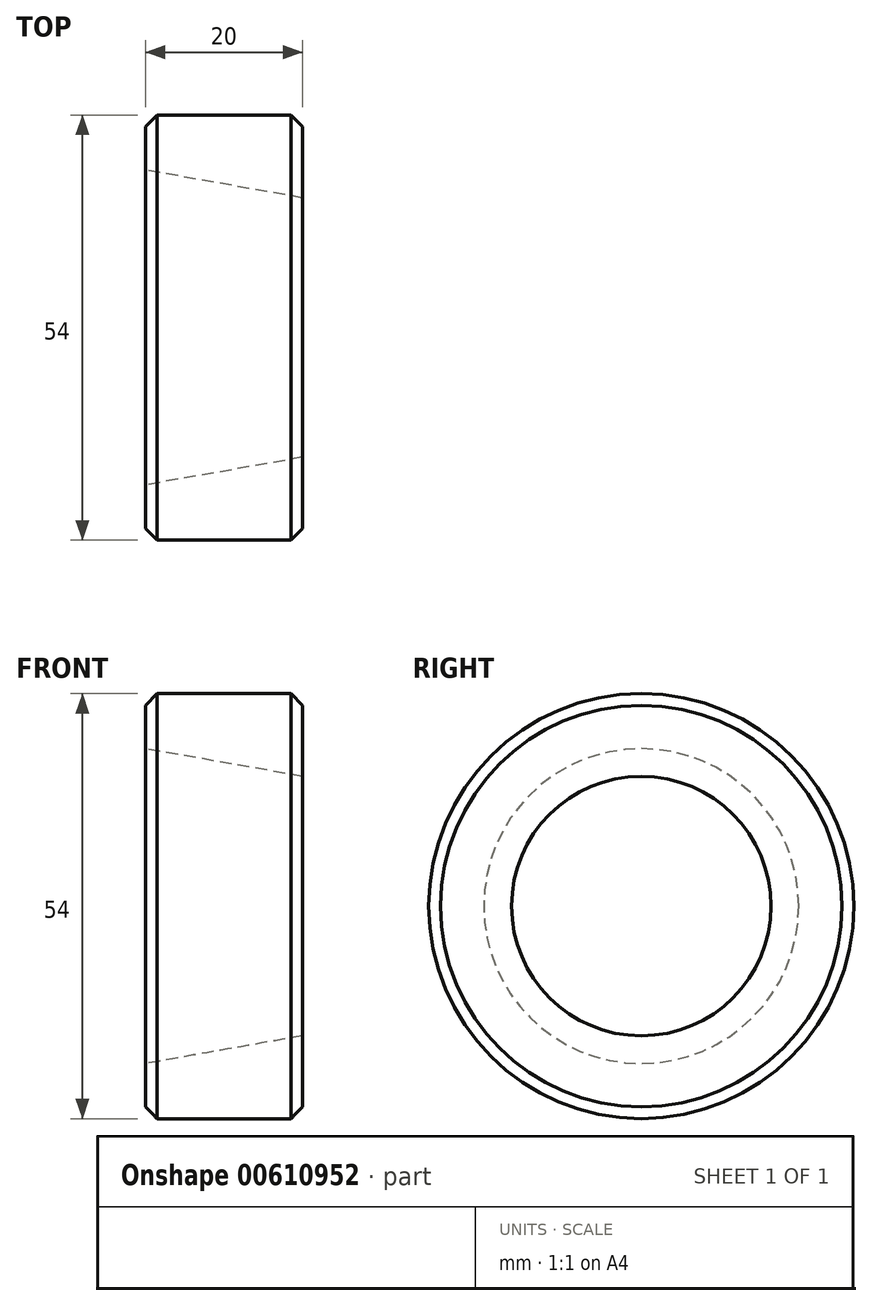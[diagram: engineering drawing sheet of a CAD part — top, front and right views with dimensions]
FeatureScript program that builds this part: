
annotation { "Feature Type Name" : "Feature", "Feature Type Description" : "" }
export const myFeature = defineFeature(function(context is Context, id is Id, definition is map)
    precondition{}
    {
        {
            var Q0;
            Q0=qCreatedBy(makeId("Front.planeOp"),FACE);
            var sketch = newSketch(context, id + "F0", { "sketchPlane" : qUnion([Q0])});
            skLineSegment(sketch, "E0.bottom", {"start": v(0, 0) * mm, "end": v(26, 0) * mm});
            skLineSegment(sketch, "E0.top", {"start": v(0, -15) * mm, "end": v(26, -15) * mm});
            skLineSegment(sketch, "E0.left", {"start": v(0, 0) * mm, "end": v(0, -15) * mm});
            skLineSegment(sketch, "E0.right", {"start": v(26, 0) * mm, "end": v(26, -15) * mm});
            skArc(sketch, "E1", {"start": v(32, -11) * mm, "mid": v(29, -9.02) * mm, "end": v(26, -11) * mm});
            skLineSegment(sketch, "E2.bottom", {"start": v(32, -15) * mm, "end": v(37, -15) * mm});
            skLineSegment(sketch, "E2.top", {"start": v(32, 0) * mm, "end": v(37, 0) * mm});
            skLineSegment(sketch, "E2.left", {"start": v(32, -15) * mm, "end": v(32, 0) * mm});
            skLineSegment(sketch, "E2.right", {"start": v(37, -15) * mm, "end": v(37, 0) * mm});
            skLineSegment(sketch, "E3", {"start": v(26, 0) * mm, "end": v(32, 0) * mm});
            skLineSegment(sketch, "E4.bottom", {"start": v(37, 0) * mm, "end": v(44, 0) * mm});
            skLineSegment(sketch, "E4.top", {"start": v(37, -10) * mm, "end": v(44, -10) * mm});
            skLineSegment(sketch, "E4.left", {"start": v(37, 0) * mm, "end": v(37, -10) * mm});
            skLineSegment(sketch, "E4.right", {"start": v(44, 0) * mm, "end": v(44, -10) * mm});
            skLineSegment(sketch, "E5.right", {"start": v(70, 0) * mm, "end": v(70, -20) * mm});
            skLineSegment(sketch, "E6", {"start": v(70, -20) * mm, "end": v(89, -16.65) * mm});
            skLineSegment(sketch, "E7", {"start": v(89, -16.65) * mm, "end": v(89, 0) * mm});
            skLineSegment(sketch, "E8", {"start": v(89, 0) * mm, "end": v(70, 0) * mm});
            skLineSegment(sketch, "E9.bottom", {"start": v(89, -13) * mm, "end": v(94, -13) * mm});
            skLineSegment(sketch, "E9.top", {"start": v(89, 0) * mm, "end": v(94, 0) * mm});
            skLineSegment(sketch, "E9.left", {"start": v(89, -13) * mm, "end": v(89, 0) * mm});
            skLineSegment(sketch, "E9.right", {"start": v(94, -13) * mm, "end": v(94, 0) * mm});
            skLineSegment(sketch, "E10.bottom", {"start": v(94, 0) * mm, "end": v(120, 0) * mm});
            skLineSegment(sketch, "E10.top", {"start": v(94, -15) * mm, "end": v(120, -15) * mm});
            skLineSegment(sketch, "E10.left", {"start": v(94, 0) * mm, "end": v(94, -15) * mm});
            skLineSegment(sketch, "E10.right", {"start": v(120, 0) * mm, "end": v(120, -15) * mm});
            skLineSegment(sketch, "E11.bottom", {"start": v(44, 0) * mm, "end": v(49, 0) * mm});
            skLineSegment(sketch, "E11.top", {"start": v(44, -15) * mm, "end": v(49, -15) * mm});
            skLineSegment(sketch, "E11.left", {"start": v(44, 0) * mm, "end": v(44, -15) * mm});
            skLineSegment(sketch, "E11.right", {"start": v(49, 0) * mm, "end": v(49, -15) * mm});
            skLineSegment(sketch, "E12.bottom", {"start": v(61, -10) * mm, "end": v(49, -10) * mm});
            skLineSegment(sketch, "E12.top", {"start": v(61, 0) * mm, "end": v(49, 0) * mm});
            skLineSegment(sketch, "E12.left", {"start": v(61, -10) * mm, "end": v(61, 0) * mm});
            skLineSegment(sketch, "E12.right", {"start": v(49, -10) * mm, "end": v(49, 0) * mm});
            skLineSegment(sketch, "E13.bottom", {"start": v(61, 0) * mm, "end": v(66, 0) * mm});
            skLineSegment(sketch, "E13.top", {"start": v(61, -34.36) * mm, "end": v(66, -34.36) * mm});
            skLineSegment(sketch, "E13.left", {"start": v(61, 0) * mm, "end": v(61, -34.36) * mm});
            skLineSegment(sketch, "E13.right", {"start": v(66, 0) * mm, "end": v(66, -34.36) * mm});
            skLineSegment(sketch, "E14.bottom", {"start": v(66, 0) * mm, "end": v(70, 0) * mm});
            skLineSegment(sketch, "E14.top", {"start": v(66, -20) * mm, "end": v(70, -20) * mm});
            skLineSegment(sketch, "E14.left", {"start": v(66, 0) * mm, "end": v(66, -20) * mm});
            skLineSegment(sketch, "E15", {"start": v(-23.07, 0) * mm, "end": v(-45.74, 0) * mm, "construction": true});
            skPoint(sketch, "E16", {"position": v(29, -9.02) * mm});
            skLineSegment(sketch, "E17", {"start": v(89, -16.65) * mm, "end": v(82.27, -16.65) * mm, "construction": true});
            skSolve(sketch);
        }
        {
            var Q0;
            Q0=qCreatedBy(makeId("Front.planeOp"),FACE);
            var sketch = newSketch(context, id + "F1", { "sketchPlane" : qUnion([Q0])});
            skLineSegment(sketch, "E18.bottom", {"start": v(70, -20) * mm, "end": v(90, -20) * mm, "construction": true});
            skLineSegment(sketch, "E18.top", {"start": v(70, -27) * mm, "end": v(90, -27) * mm});
            skLineSegment(sketch, "E18.left", {"start": v(70, -20) * mm, "end": v(70, -27) * mm});
            skLineSegment(sketch, "E18.right", {"start": v(90, -20) * mm, "end": v(90, -27) * mm});
            skLineSegment(sketch, "E19", {"start": v(70, -20) * mm, "end": v(90, -16.47) * mm});
            skLineSegment(sketch, "E20.MirrorCS", {"start": v(70, 20) * mm, "end": v(90, 16.47) * mm});
            skLineSegment(sketch, "E21", {"start": v(90, -20) * mm, "end": v(90, -16.47) * mm});
            skSolve(sketch);
        }
        {
            var Q0;
            Q0=makeQuery(id+"F1.imprint","IMPRINT",FACE,{"disambiguationData":[TD([[makeQuery(id+"F1.imprint","IMPRINT",EDGE,{"derivedFrom":sQuery(id+"F1.wireOp",EDGE,"E18.top")}),1.0]])]});
            var Q1;
            Q1=sQuery(id+"F0.wireOp",EDGE,"E8");
            revolve(context, id + "F2", {"entities" : qUnion([Q0]), "axis" : qUnion([Q1]), "revolveType" : RevolveType.FULL});
        }
        {
            var Q0;
            Q0=makeQuery(id+"F2.opRevolve","SWEPT_EDGE",EDGE,{"disambiguationData":[OSD([sQuery(id+"F1.wireOp",EDGE,"E18.top"),sQuery(id+"F1.wireOp",EDGE,"E18.left")])]});
            var Q1;
            Q1=makeQuery(id+"F2.opRevolve","SWEPT_EDGE",EDGE,{"disambiguationData":[OSD([sQuery(id+"F1.wireOp",EDGE,"E18.top"),sQuery(id+"F1.wireOp",EDGE,"E18.right")])]});
            chamfer(context, id + "F3", {"entities" : qUnion([Q0, Q1]), "width" : 1.5 * mm, "tangentPropagation" : true});
        }
    });
